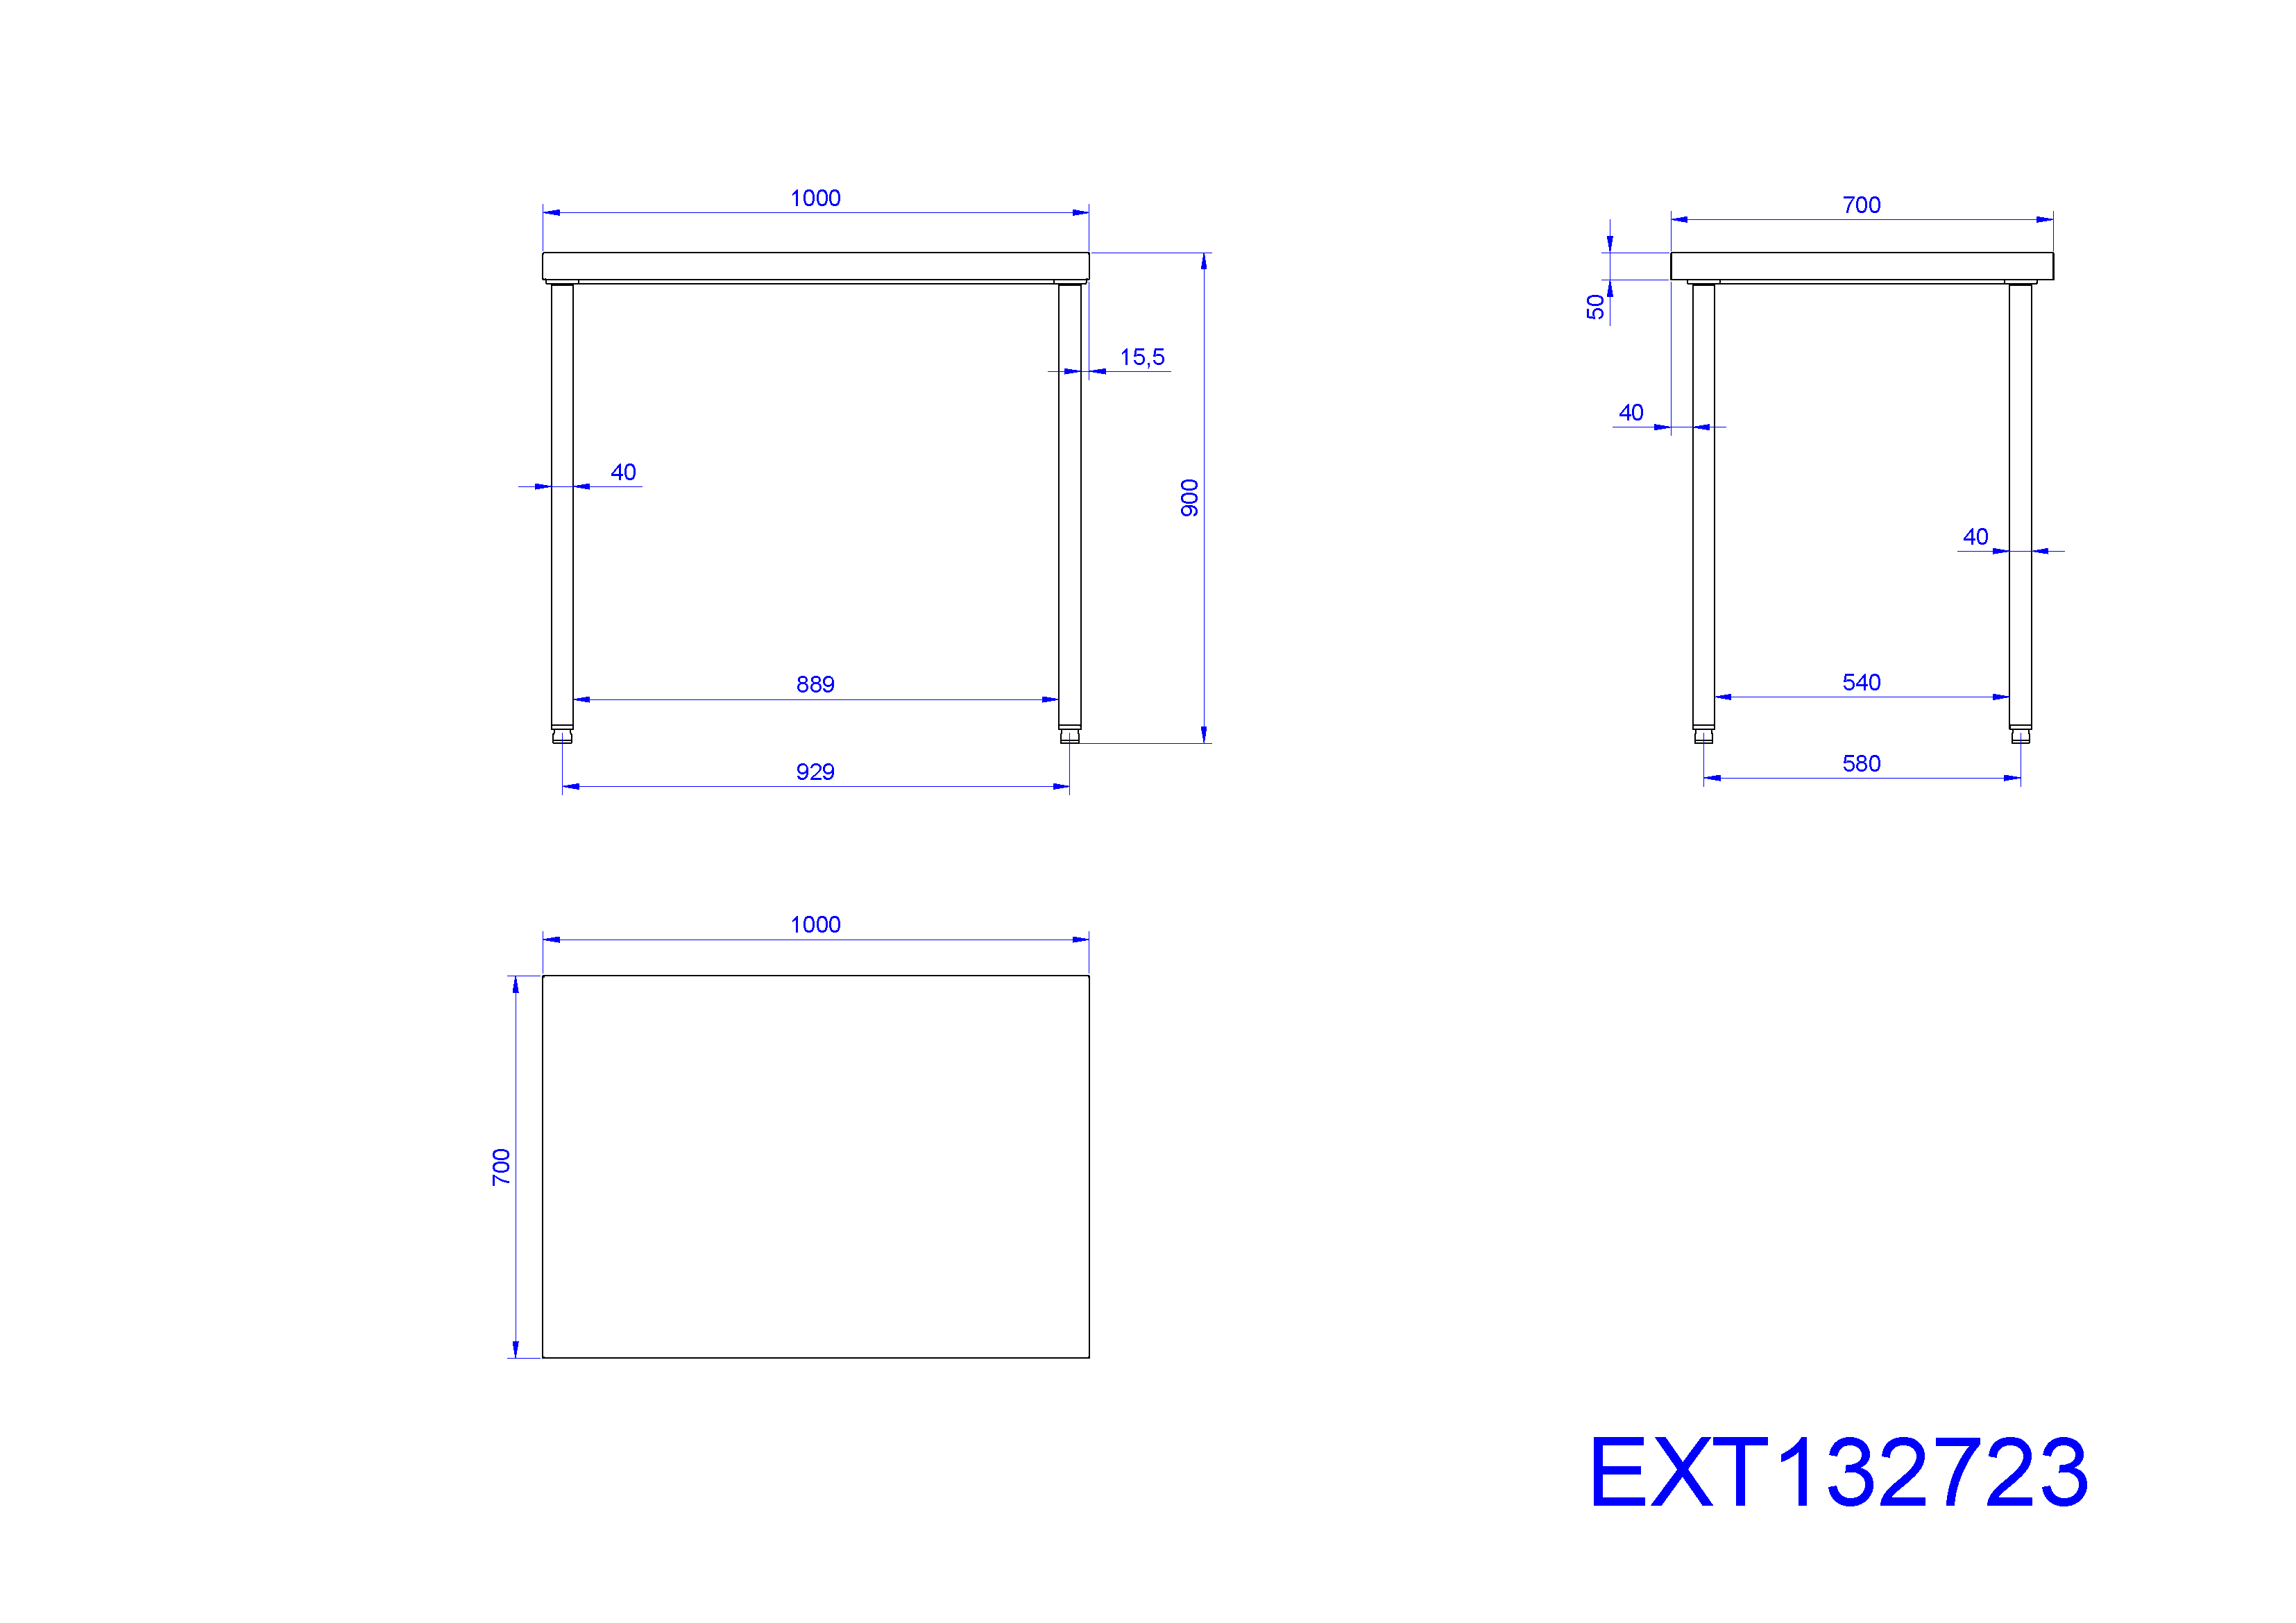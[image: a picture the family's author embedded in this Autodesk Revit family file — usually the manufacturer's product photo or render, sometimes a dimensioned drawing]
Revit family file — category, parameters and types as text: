
# Revit family: QF_ZANUSSI_132729_TG2400PN
name_source: partatom
category: Attrezzature speciali
units: mm (PartAtom-declared; Revit-internal decimal feet)

## family parameters
Basato su piano di lavoro = No
Condiviso = No
Punto di calcolo locali = No
Quota connettore circolare = Usa diametro
Sempre verticale = Sì
Taglio con vuoti quando caricato = No
Tipo di parte = Normale

## types (1)
- Standard
    Accessory = Sì
    Cold Water Size = 0 mm
    Compressed Air Pressure = 0.0 Pa
    Compressed Air Size = 0 mm
    Compressed Air Volume = 0.0 L/s
    Condensate Return Size = 0 mm
    Cycle = 0 Hz
    Depth Actual = 700 mm  [stored 2.29659 ft]
    Descrizione = WORK TABLE 2400 MM
    Direct Waste Size = 0 mm
    Gas Input Pressure = 0
    Gas KW = 0
    Gas Size = 0 mm
    HP = 0 HP
    Height Actual = 900 mm  [stored 2.95276 ft]
    Hot Water Size = 0 mm
    Item Number = 132729
    Length Actual = 2400 mm  [stored 7.87402 ft]
    Modello = TG2400PN
    Phase = 0
    Produttore = Zanussi
    Prospetto di default = 0 mm  [stored 0 ft]
    Refrigerant Compressor Remote = Sì
    Refrigeration Liquid Line Size = 0 mm  [stored 0 ft]
    Refrigeration Suction Line Size = 0 mm  [stored 0 ft]
    Steam Consumption per Hour = 0
    Steam Supply Maximum Pressure = 0.0 Pa
    Steam Supply Minimum Pressure = 0.0 Pa
    Steam Supply Size = 0 mm
    URL = http://www.zanussiprofessional.com
    URL Manufacturer = http://www.zanussiprofessional.com
    Volts = 0 V
    Watts = 0 W
    Weight = 84.00 kg

note: source unit labels omitted for Gas Input Pressure — the stored unit's dimension contradicts the parameter name (converter mislabeling)

note: [stored X ft] marks values corroborated as IEEE doubles in the binary element streams (Revit-internal decimal feet)

## geometry (parser evidence)
native form markers: Sweep x2
no freeform markers — native parametric forms only
